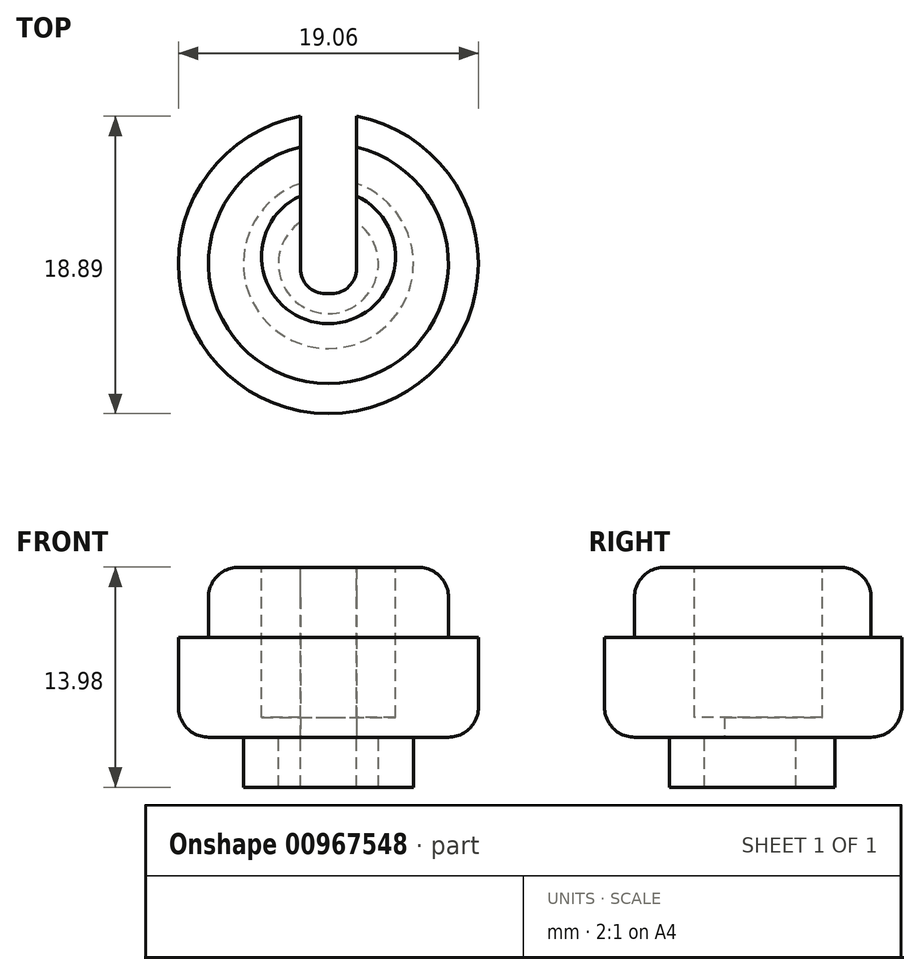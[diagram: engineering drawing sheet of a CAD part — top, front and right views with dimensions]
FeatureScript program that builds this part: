
annotation { "Feature Type Name" : "Feature", "Feature Type Description" : "" }
export const myFeature = defineFeature(function(context is Context, id is Id, definition is map)
    precondition{}
    {
        {
            var Q0;
            Q0=qCreatedBy(makeId("Top.planeOp"),FACE);
            var sketch = newSketch(context, id + "F0", { "sketchPlane" : qUnion([Q0])});
            skCircle(sketch, "E0", {"center": v(0, 0) * mm, "radius": 9.53 * mm});
            skSolve(sketch);
        }
        {
            var Q0;
            Q0=makeQuery(id+"F0.imprint","IMPRINT",FACE,{"disambiguationData":[TD([[makeQuery(id+"F0.imprint","IMPRINT",EDGE,{"derivedFrom":sQuery(id+"F0.wireOp",EDGE,"E0")}),1.0]])]});
            extrude(context, id + "F1", {"entities" : qUnion([Q0]), "depth" : 6.35 * mm, "offsetDistance" : 25.4 * mm});
        }
        {
            var Q0;
            Q0=makeQuery(id+"F1.opExtrude","CAP_FACE",FACE,{"disambiguationData":[OSD([sQuery(id+"F0.wireOp",EDGE,"E0")])],"isStart":false});
            var sketch = newSketch(context, id + "F2", { "sketchPlane" : qUnion([Q0])});
            skCircle(sketch, "E1", {"center": v(0, 0) * mm, "radius": 7.62 * mm});
            skSolve(sketch);
        }
        {
            var Q0;
            Q0 = qSketchRegion(id + "F2", true);
            extrude(context, id + "F3", {"entities" : qUnion([Q0]), "operationType" : NewBodyOperationType.ADD, "depth" : 4.44 * mm, "offsetDistance" : 25.4 * mm});
        }
        {
            var Q0;
            Q0=makeQuery(id+"F1.opExtrude","CAP_FACE",FACE,{"disambiguationData":[OSD([sQuery(id+"F0.wireOp",EDGE,"E0")])],"isStart":true});
            var sketch = newSketch(context, id + "F4", { "sketchPlane" : qUnion([Q0])});
            skCircle(sketch, "E2", {"center": v(0, 0) * mm, "radius": 3.18 * mm});
            skCircle(sketch, "E3", {"center": v(0, 0) * mm, "radius": 5.4 * mm});
            skSolve(sketch);
        }
        {
            var Q0;
            Q0=makeQuery(id+"F4.imprint","IMPRINT",FACE,{"disambiguationData":[TD([[makeQuery(id+"F4.imprint","IMPRINT",EDGE,{"derivedFrom":sQuery(id+"F4.wireOp",EDGE,"E2")}),-1.0]])]});
            extrude(context, id + "F5", {"entities" : qUnion([Q0]), "operationType" : NewBodyOperationType.ADD, "depth" : 3.17 * mm, "offsetDistance" : 25.4 * mm});
        }
        {
            var Q0;
            Q0=qCreatedBy(makeId("Front.planeOp"),FACE);
            var sketch = newSketch(context, id + "F6", { "sketchPlane" : qUnion([Q0])});
            skLineSegment(sketch, "E4.bottom", {"start": v(-1.78, 13.34) * mm, "end": v(1.78, 13.34) * mm});
            skLineSegment(sketch, "E4.top", {"start": v(-1.78, -12.07) * mm, "end": v(1.78, -12.07) * mm});
            skLineSegment(sketch, "E4.left", {"start": v(-1.78, 13.34) * mm, "end": v(-1.78, -12.07) * mm});
            skLineSegment(sketch, "E4.right", {"start": v(1.78, 13.34) * mm, "end": v(1.78, -12.07) * mm});
            skSolve(sketch);
        }
        {
            var Q0;
            Q0 = qSketchRegion(id + "F6", true);
            extrude(context, id + "F7", {"entities" : qUnion([Q0]), "operationType" : NewBodyOperationType.REMOVE, "oppositeDirection" : true, "depth" : 12.7 * mm, "offsetDistance" : 25.4 * mm});
        }
        {
            var Q0;
            Q0=makeQuery(id+"F7.boolean.opBoolean","COPY",FACE,{"derivedFrom":makeQuery(id+"F7.opExtrude","CAP_FACE",FACE,{"disambiguationData":[OSD([sQuery(id+"F6.wireOp",EDGE,"E4.bottom"),sQuery(id+"F6.wireOp",EDGE,"E4.top"),sQuery(id+"F6.wireOp",EDGE,"E4.left"),sQuery(id+"F6.wireOp",EDGE,"E4.right")])],"isStart":true})});
            var sketch = newSketch(context, id + "F8", { "sketchPlane" : qUnion([Q0])});
            skLineSegment(sketch, "E5.bottom", {"start": v(1.78, 0) * mm, "end": v(-1.78, 0) * mm});
            skLineSegment(sketch, "E5.top", {"start": v(1.78, 10.8) * mm, "end": v(-1.78, 10.8) * mm});
            skLineSegment(sketch, "E5.left", {"start": v(1.78, 0) * mm, "end": v(1.78, 10.8) * mm});
            skLineSegment(sketch, "E5.right", {"start": v(-1.78, 0) * mm, "end": v(-1.78, 10.8) * mm});
            skSolve(sketch);
        }
        {
            var Q0;
            Q0 = qSketchRegion(id + "F8", true);
            extrude(context, id + "F9", {"entities" : qUnion([Q0]), "operationType" : NewBodyOperationType.REMOVE, "oppositeDirection" : true, "depth" : 1.9 * mm, "offsetDistance" : 25.4 * mm});
        }
        {
            var Q0;
            Q0=makeQuery(id+"F9.boolean.opBoolean","COPY",EDGE,{"derivedFrom":makeQuery(id+"F9.opExtrude","CAP_EDGE",EDGE,{"disambiguationData":[OSD([sQuery(id+"F8.wireOp",EDGE,"E5.left")])],"isStart":false})});
            var Q1;
            Q1=makeQuery(id+"F9.boolean.opBoolean","COPY",EDGE,{"derivedFrom":makeQuery(id+"F9.opExtrude","CAP_EDGE",EDGE,{"disambiguationData":[OSD([sQuery(id+"F8.wireOp",EDGE,"E5.right")])],"isStart":false})});
            fillet(context, id + "F10", {"entities" : qUnion([Q0, Q1]), "radius" : 1.59 * mm, "tangentPropagation" : true, "allowEdgeOverflow" : false});
        }
        {
            var Q0;
            Q0=makeQuery(id+"F5.opExtrude","CAP_EDGE",EDGE,{"disambiguationData":[OSD([sQuery(id+"F4.wireOp",EDGE,"E3")])],"isStart":true});
            var Q1;
            Q1=makeQuery(id+"F1.opExtrude","CAP_EDGE",EDGE,{"disambiguationData":[OSD([sQuery(id+"F0.wireOp",EDGE,"E0")])],"isStart":true});
            var Q2;
            Q2=makeQuery(id+"F3.opExtrude","CAP_EDGE",EDGE,{"disambiguationData":[OSD([sQuery(id+"F2.wireOp",EDGE,"E1")])],"isStart":false});
            fillet(context, id + "F11", {"entities" : qUnion([Q0, Q1, Q2]), "radius" : 1.9 * mm, "tangentPropagation" : true, "allowEdgeOverflow" : false});
        }
        {
            var Q0;
            Q0=makeQuery(id+"F3.opExtrude","CAP_FACE",FACE,{"disambiguationData":[OSD([sQuery(id+"F2.wireOp",EDGE,"E1")])],"isStart":false});
            var sketch = newSketch(context, id + "F12", { "sketchPlane" : qUnion([Q0])});
            skCircle(sketch, "E6", {"center": v(0, 0.44) * mm, "radius": 4.25 * mm});
            skSolve(sketch);
        }
        {
            var Q0;
            Q0 = qSketchRegion(id + "F12", true);
            extrude(context, id + "F13", {"entities" : qUnion([Q0]), "operationType" : NewBodyOperationType.REMOVE, "oppositeDirection" : true, "depth" : 9.52 * mm, "offsetDistance" : 25.4 * mm});
        }
    });
